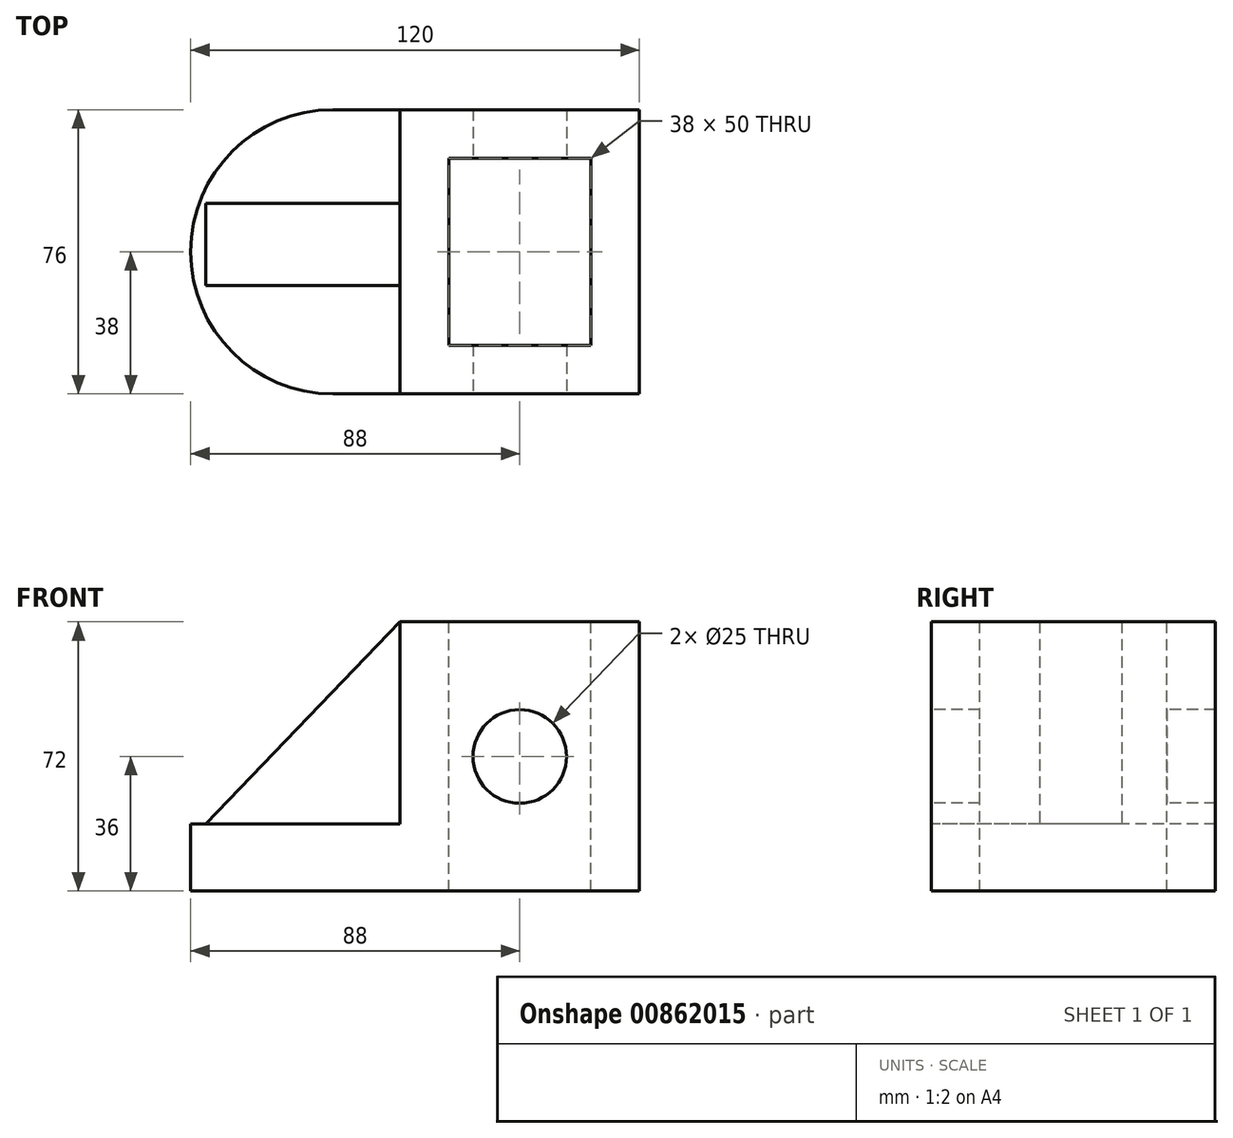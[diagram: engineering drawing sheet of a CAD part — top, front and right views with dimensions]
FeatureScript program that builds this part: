
annotation { "Feature Type Name" : "Feature", "Feature Type Description" : "" }
export const myFeature = defineFeature(function(context is Context, id is Id, definition is map)
    precondition{}
    {
        {
            var Q0;
            Q0=qCreatedBy(makeId("Front.planeOp"),FACE);
            var sketch = newSketch(context, id + "F0", { "sketchPlane" : qUnion([Q0])});
            skLineSegment(sketch, "E0", {"start": v(0, 0) * mm, "end": v(120, 0) * mm});
            skLineSegment(sketch, "E1", {"start": v(120, 0) * mm, "end": v(120, 72) * mm});
            skLineSegment(sketch, "E2", {"start": v(120, 72) * mm, "end": v(56, 72) * mm});
            skLineSegment(sketch, "E3", {"start": v(56, 72) * mm, "end": v(56, 18) * mm});
            skLineSegment(sketch, "E4", {"start": v(56, 18) * mm, "end": v(0, 18) * mm});
            skLineSegment(sketch, "E5", {"start": v(0, 18) * mm, "end": v(0, 0) * mm});
            skCircle(sketch, "E6", {"center": v(88, 36) * mm, "radius": 12.5 * mm});
            skPoint(sketch, "E6.centerSnap0", {"position": v(120, 36) * mm});
            skPoint(sketch, "E6.centerSnap1", {"position": v(88, 72) * mm});
            skSolve(sketch);
        }
        {
            var Q0;
            Q0=makeQuery(id+"F0.imprint","IMPRINT",FACE,{"disambiguationData":[TD([[makeQuery(id+"F0.imprint","IMPRINT",EDGE,{"derivedFrom":sQuery(id+"F0.wireOp",EDGE,"E0")}),1.0]])]});
            extrude(context, id + "F1", {"entities" : qUnion([Q0]), "oppositeDirection" : true, "depth" : 76 * mm, "offsetDistance" : 25 * mm});
        }
        {
            var Q0;
            Q0=makeQuery(id+"F1.opExtrude","SWEPT_FACE",FACE,{"disambiguationData":[OSD([sQuery(id+"F0.wireOp",EDGE,"E2")])]});
            var sketch = newSketch(context, id + "F2", { "sketchPlane" : qUnion([Q0])});
            skLineSegment(sketch, "E7", {"start": v(107, 63) * mm, "end": v(69, 63) * mm});
            skLineSegment(sketch, "E8", {"start": v(69, 63) * mm, "end": v(69, 13) * mm});
            skLineSegment(sketch, "E9", {"start": v(69, 13) * mm, "end": v(107, 13) * mm});
            skLineSegment(sketch, "E10", {"start": v(107, 63) * mm, "end": v(107, 13) * mm});
            skSolve(sketch);
        }
        {
            var Q0;
            Q0=makeQuery(id+"F2.imprint","IMPRINT",FACE,{"disambiguationData":[TD([[makeQuery(id+"F2.imprint","IMPRINT",EDGE,{"derivedFrom":sQuery(id+"F2.wireOp",EDGE,"E7")}),1.0]])]});
            extrude(context, id + "F3", {"entities" : qUnion([Q0]), "operationType" : NewBodyOperationType.REMOVE, "oppositeDirection" : true, "depth" : 98.3 * mm, "offsetDistance" : 25 * mm});
        }
        {
            var Q0;
            Q0=makeQuery(id+"F1.opExtrude","SWEPT_FACE",FACE,{"disambiguationData":[OSD([sQuery(id+"F0.wireOp",EDGE,"E4")])]});
            var sketch = newSketch(context, id + "F4", { "sketchPlane" : qUnion([Q0])});
            skArc(sketch, "E11", {"start": v(38, 76) * mm, "mid": v(0, 38) * mm, "end": v(38, 0) * mm});
            skSolve(sketch);
        }
        {
            var Q0;
            {var subQ0=sQuery(id+"F4.wireOp",EDGE,"E11");var subQ1=sQuery(id+"F0.wireOp",EDGE,"E4");var subQ2=makeQuery(id+"F1.opExtrude","CAP_EDGE",EDGE,{"disambiguationData":[OSD([subQ1])],"isStart":false});var subQ3=makeQuery(id+"F4.imprint","INTERSECT",VERTEX,{"derivedFrom":[subQ2,subQ0]});Q0=makeQuery(id+"F4.imprint","IMPRINT",FACE,{"disambiguationData":[TD([[makeQuery(id+"F4.imprint","IMPRINT",EDGE,{"disambiguationData":[TD([[subQ3,-1.0]])],"derivedFrom":subQ0}),-1.0]])]});}
            var Q1;
            {var subQ0=sQuery(id+"F4.wireOp",EDGE,"E11");var subQ1=sQuery(id+"F0.wireOp",EDGE,"E4");var subQ2=makeQuery(id+"F1.opExtrude","CAP_EDGE",EDGE,{"disambiguationData":[OSD([subQ1])],"isStart":true});var subQ3=makeQuery(id+"F4.imprint","INTERSECT",VERTEX,{"derivedFrom":[subQ2,subQ0]});Q1=makeQuery(id+"F4.imprint","IMPRINT",FACE,{"disambiguationData":[TD([[makeQuery(id+"F4.imprint","IMPRINT",EDGE,{"disambiguationData":[TD([[subQ3,1.0]])],"derivedFrom":subQ0}),-1.0]])]});}
            extrude(context, id + "F5", {"entities" : qUnion([Q0, Q1]), "operationType" : NewBodyOperationType.REMOVE, "oppositeDirection" : true, "depth" : 25 * mm, "offsetDistance" : 25 * mm});
        }
        {
            var Q0;
            Q0=makeQuery(id+"F1.opExtrude","SWEPT_FACE",FACE,{"disambiguationData":[OSD([sQuery(id+"F0.wireOp",EDGE,"E4")])]});
            var sketch = newSketch(context, id + "F6", { "sketchPlane" : qUnion([Q0])});
            skLineSegment(sketch, "E12", {"start": v(56, 76) * mm, "end": v(56, 40) * mm});
            skLineSegment(sketch, "E13", {"start": v(56, 40) * mm, "end": v(56, 51) * mm});
            skLineSegment(sketch, "E14", {"start": v(56, 51) * mm, "end": v(56, 29) * mm});
            skLineSegment(sketch, "E15", {"start": v(56, 29) * mm, "end": v(4, 29) * mm});
            skLineSegment(sketch, "E16", {"start": v(56, 51) * mm, "end": v(4, 51) * mm});
            skLineSegment(sketch, "E17", {"start": v(4, 51) * mm, "end": v(4, 29) * mm});
            skSolve(sketch);
        }
        {
            var Q0;
            {var subQ2=sQuery(id+"F6.wireOp",EDGE,"E15");Q0=makeQuery(id+"F6.imprint","IMPRINT",FACE,{"disambiguationData":[TD([[makeQuery(id+"F6.imprint","IMPRINT",EDGE,{"derivedFrom":subQ2}),-1.0]])]});}
            extrude(context, id + "F7", {"entities" : qUnion([Q0]), "operationType" : NewBodyOperationType.ADD, "depth" : 54 * mm, "offsetDistance" : 25 * mm});
        }
        {
            var Q0;
            Q0=makeQuery(id+"F7.opExtrude","SWEPT_FACE",FACE,{"disambiguationData":[OSD([sQuery(id+"F6.wireOp",EDGE,"E15")])]});
            var sketch = newSketch(context, id + "F8", { "sketchPlane" : qUnion([Q0])});
            skLineSegment(sketch, "E18", {"start": v(56, 72) * mm, "end": v(4, 18) * mm});
            skLineSegment(sketch, "E19", {"start": v(4, 18) * mm, "end": v(4, 72) * mm});
            skLineSegment(sketch, "E20", {"start": v(4, 72) * mm, "end": v(56, 72) * mm});
            skSolve(sketch);
        }
        {
            var Q0;
            Q0=makeQuery(id+"F8.imprint","IMPRINT",FACE,{"disambiguationData":[TD([[makeQuery(id+"F8.imprint","IMPRINT",EDGE,{"derivedFrom":sQuery(id+"F8.wireOp",EDGE,"E18")}),-1.0]])]});
            extrude(context, id + "F9", {"entities" : qUnion([Q0]), "operationType" : NewBodyOperationType.REMOVE, "oppositeDirection" : true, "depth" : 44.5 * mm, "offsetDistance" : 25 * mm});
        }
    });
